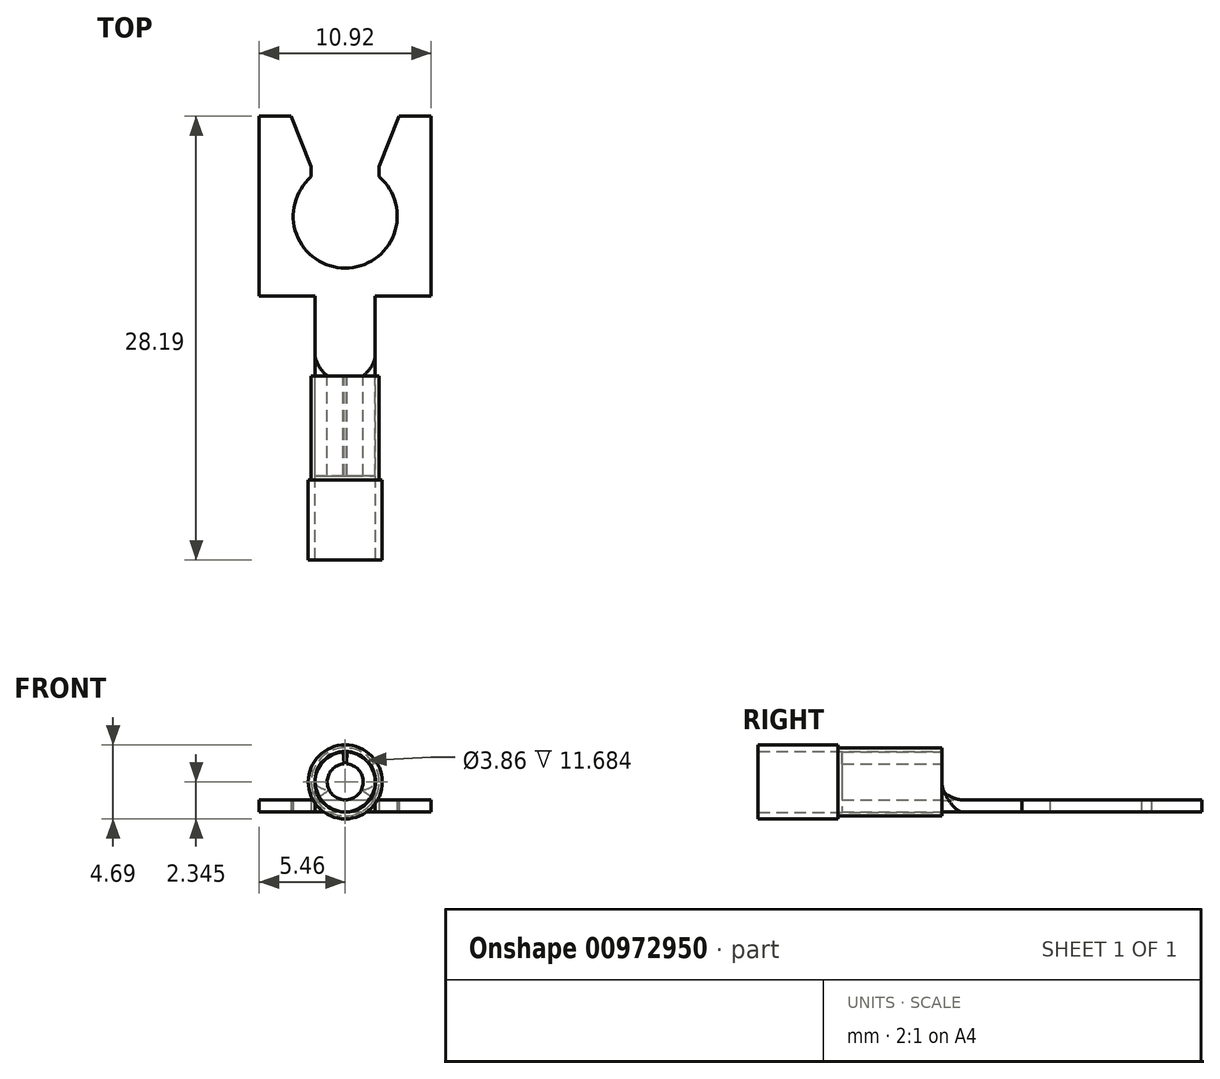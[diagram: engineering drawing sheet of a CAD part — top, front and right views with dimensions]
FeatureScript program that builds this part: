
annotation { "Feature Type Name" : "Feature", "Feature Type Description" : "" }
export const myFeature = defineFeature(function(context is Context, id is Id, definition is map)
    precondition{}
    {
        {
            var Q0;
            Q0=qCreatedBy(makeId("Top.planeOp"),FACE);
            var sketch = newSketch(context, id + "F0", { "sketchPlane" : qUnion([Q0])});
            skLineSegment(sketch, "E0.bottom", {"start": v(-5.46, 6.35) * mm, "end": v(-3.43, 6.35) * mm});
            skLineSegment(sketch, "E0.top", {"start": v(-5.46, -5.08) * mm, "end": v(5.46, -5.08) * mm});
            skLineSegment(sketch, "E0.left", {"start": v(-5.46, 6.35) * mm, "end": v(-5.46, -5.08) * mm});
            skLineSegment(sketch, "E0.right", {"start": v(5.46, 6.35) * mm, "end": v(5.46, -5.08) * mm});
            skArc(sketch, "E1", {"start": v(-2.16, 2.5) * mm, "mid": v(0, -3.3) * mm, "end": v(2.16, 2.5) * mm});
            skLineSegment(sketch, "E2.bottom", {"start": v(-1.9, -5.08) * mm, "end": v(1.9, -5.08) * mm});
            skLineSegment(sketch, "E2.top", {"start": v(-1.9, -8.9) * mm, "end": v(1.9, -8.9) * mm});
            skLineSegment(sketch, "E2.left", {"start": v(-1.9, -5.08) * mm, "end": v(-1.9, -8.9) * mm});
            skLineSegment(sketch, "E2.right", {"start": v(1.9, -5.08) * mm, "end": v(1.9, -8.9) * mm});
            skPoint(sketch, "E3", {"position": v(0, -5.08) * mm});
            skLineSegment(sketch, "E4.trimOffspring", {"start": v(3.43, 6.35) * mm, "end": v(5.46, 6.35) * mm});
            skLineSegment(sketch, "E5", {"start": v(-3.43, 6.35) * mm, "end": v(-2.16, 3.13) * mm});
            skLineSegment(sketch, "E6", {"start": v(-2.16, 3.13) * mm, "end": v(-2.16, 2.5) * mm});
            skLineSegment(sketch, "E7", {"start": v(3.43, 6.35) * mm, "end": v(2.16, 3.13) * mm});
            skLineSegment(sketch, "E8", {"start": v(2.16, 3.13) * mm, "end": v(2.16, 2.5) * mm});
            skSolve(sketch);
        }
        {
            var Q0;
            Q0 = qSketchRegion(id + "F0", true);
            extrude(context, id + "F1", {"entities" : qUnion([Q0]), "depth" : 0.76 * mm, "offsetDistance" : 25.4 * mm});
        }
        {
            var Q0;
            {var subQ0=sQuery(id+"F0.wireOp",EDGE,"E2.left");var subQ1=sQuery(id+"F0.wireOp",EDGE,"E2.top");var subQ2=makeQuery(id+"F1.opExtrude","SWEPT_FACE",FACE,{"disambiguationData":[OSD([subQ1])]});Q0=makeQuery(id+"F4.boolean.opBoolean","SPLIT",FACE,{"disambiguationData":[TD([makeQuery(id+"F1.opExtrude","SWEPT_FACE",FACE,{"disambiguationData":[OSD([subQ0])]})])],"derivedFrom":subQ2});}
            cPlane(context, id + "F2", {"entities" : qUnion([Q0]), "cplaneType" : CPlaneType.OFFSET, "offset" : 1.27 * mm, "width" : 152.4 * mm, "height" : 152.4 * mm});
        }
        {
            var Q0;
            Q0=qCreatedBy(id+"F2.planeOp",FACE);
            var sketch = newSketch(context, id + "F3", { "sketchPlane" : qUnion([Q0])});
            skArc(sketch, "E9", {"start": v(-0.13, 3.8) * mm, "mid": v(0, 0) * mm, "end": v(0.13, 3.8) * mm});
            skArc(sketch, "E10", {"start": v(-0.08, 3.05) * mm, "mid": v(0, 0.76) * mm, "end": v(0.08, 3.05) * mm});
            skLineSegment(sketch, "E11", {"start": v(0, 1.9) * mm, "end": v(0, 0) * mm, "construction": true});
            skLineSegment(sketch, "E12", {"start": v(0.08, 3.05) * mm, "end": v(0.13, 3.8) * mm});
            skLineSegment(sketch, "E13", {"start": v(-0.08, 3.05) * mm, "end": v(-0.13, 3.8) * mm});
            skLineSegment(sketch, "E14", {"start": v(-0.08, 3.05) * mm, "end": v(0.08, 3.05) * mm, "construction": true});
            skLineSegment(sketch, "E15", {"start": v(-0.13, 3.8) * mm, "end": v(0.13, 3.8) * mm, "construction": true});
            skLineSegment(sketch, "E16", {"start": v(0, 1.9) * mm, "end": v(-0.08, 3.05) * mm, "construction": true});
            skSolve(sketch);
        }
        {
            var Q0;
            Q0 = qSketchRegion(id + "F3", true);
            extrude(context, id + "F4", {"entities" : qUnion([Q0]), "operationType" : NewBodyOperationType.ADD, "depth" : 6.35 * mm, "offsetDistance" : 25.4 * mm});
        }
        {
            var Q0;
            Q0=makeQuery(id+"F4.opExtrude","CAP_FACE",FACE,{"disambiguationData":[OSD([sQuery(id+"F3.wireOp",EDGE,"E9"),sQuery(id+"F3.wireOp",EDGE,"E10"),sQuery(id+"F3.wireOp",EDGE,"E12"),sQuery(id+"F3.wireOp",EDGE,"E13")])],"isStart":true});
            var sketch = newSketch(context, id + "F5", { "sketchPlane" : qUnion([Q0])});
            skPoint(sketch, "E17.orphan", {"position": v(3.3, 0.76) * mm});
            skPoint(sketch, "E18.orphan", {"position": v(-3.3, 0.76) * mm});
            skPoint(sketch, "E19.orphan", {"position": v(0.13, 3.8) * mm});
            skPoint(sketch, "E20.orphan", {"position": v(0.08, 3.05) * mm});
            skPoint(sketch, "E21.orphan", {"position": v(-0.08, 3.05) * mm});
            skPoint(sketch, "E22.orphan", {"position": v(-0.13, 3.8) * mm});
            skLineSegment(sketch, "E23", {"start": v(1.02, 1.4) * mm, "end": v(-1.02, 1.4) * mm, "construction": true});
            skLineSegment(sketch, "E24", {"start": v(1.9, 1.78) * mm, "end": v(-1.9, 1.78) * mm, "construction": true});
            skLineSegment(sketch, "E25", {"start": v(0, 1.9) * mm, "end": v(0, 1.78) * mm, "construction": true});
            skArc(sketch, "E26", {"start": v(1.02, 1.4) * mm, "mid": v(1.5, 1.5) * mm, "end": v(1.9, 1.78) * mm});
            skArc(sketch, "E27", {"start": v(-1.9, 1.78) * mm, "mid": v(-1.5, 1.5) * mm, "end": v(-1.02, 1.4) * mm});
            skArc(sketch, "E28.0", {"start": v(0.13, 3.8) * mm, "mid": v(0, 0) * mm, "end": v(-0.13, 3.8) * mm, "construction": true});
            skSolve(sketch);
        }
        {
            var Q0;
            Q0=makeQuery(id+"F1.opExtrude","SWEPT_FACE",FACE,{"disambiguationData":[OSD([sQuery(id+"F0.wireOp",EDGE,"E2.top")])]});
            var Q1;
            {var subQ0=sQuery(id+"F5.wireOp",EDGE,"E26");Q1=makeQuery(id+"F5.imprint","IMPRINT",FACE,{"disambiguationData":[TD([[makeQuery(id+"F5.imprint","IMPRINT",EDGE,{"derivedFrom":subQ0}),-1.0]])]});}
            loft(context, id + "F6", {"operationType" : NewBodyOperationType.ADD, "startCondition" : LoftEndDerivativeType.NORMAL_TO_PROFILE, "startMagnitude" : 1, "endCondition" : LoftEndDerivativeType.TANGENT_TO_PROFILE, "endMagnitude" : 1, "sheetProfilesArray" : [{ "sheetProfileEntities" : qUnion([Q0]) }, { "sheetProfileEntities" : qUnion([Q1]) }]});
        }
        {
            var Q0;
            {var subQ0=sQuery(id+"F3.wireOp",EDGE,"E10");var subQ2=sQuery(id+"F3.wireOp",EDGE,"E9");var subQ5=sQuery(id+"F3.wireOp",EDGE,"E13");Q0=makeQuery(id+"F6.boolean.opBoolean","SPLIT",FACE,{"disambiguationData":[TD([makeQuery(id+"F4.opExtrude","SWEPT_FACE",FACE,{"disambiguationData":[OSD([subQ5])]})])],"derivedFrom":makeQuery(id+"F4.opExtrude","CAP_FACE",FACE,{"disambiguationData":[OSD([subQ2,subQ0,sQuery(id+"F3.wireOp",EDGE,"E12"),subQ5])],"isStart":true})});}
            var sketch = newSketch(context, id + "F7", { "sketchPlane" : qUnion([Q0])});
            skArc(sketch, "E29.0", {"start": v(1.9, 1.78) * mm, "mid": v(1.43, 3.16) * mm, "end": v(0.13, 3.8) * mm, "construction": true});
            skCircle(sketch, "E30", {"center": v(0, 1.9) * mm, "radius": 1.93 * mm});
            skCircle(sketch, "E31", {"center": v(0, 1.9) * mm, "radius": 2.16 * mm});
            skSolve(sketch);
        }
        {
            var Q0;
            Q0 = qSketchRegion(id + "F7", true);
            extrude(context, id + "F8", {"entities" : qUnion([Q0]), "oppositeDirection" : true, "depth" : 11.68 * mm, "offsetDistance" : 25.4 * mm});
        }
        {
            var Q0;
            Q0=makeQuery(id+"F8.opExtrude","CAP_FACE",FACE,{"disambiguationData":[OSD([sQuery(id+"F7.wireOp",EDGE,"E30"),sQuery(id+"F7.wireOp",EDGE,"E31")])],"isStart":false});
            var sketch = newSketch(context, id + "F9", { "sketchPlane" : qUnion([Q0])});
            skCircle(sketch, "E32.0", {"center": v(0, 1.9) * mm, "radius": 1.93 * mm});
            skCircle(sketch, "E33", {"center": v(0, 1.9) * mm, "radius": 2.35 * mm});
            skSolve(sketch);
        }
        {
            var Q0;
            Q0 = qSketchRegion(id + "F9", true);
            extrude(context, id + "F10", {"entities" : qUnion([Q0]), "operationType" : NewBodyOperationType.ADD, "oppositeDirection" : true, "depth" : 5.08 * mm, "offsetDistance" : 25.4 * mm});
        }
    });
